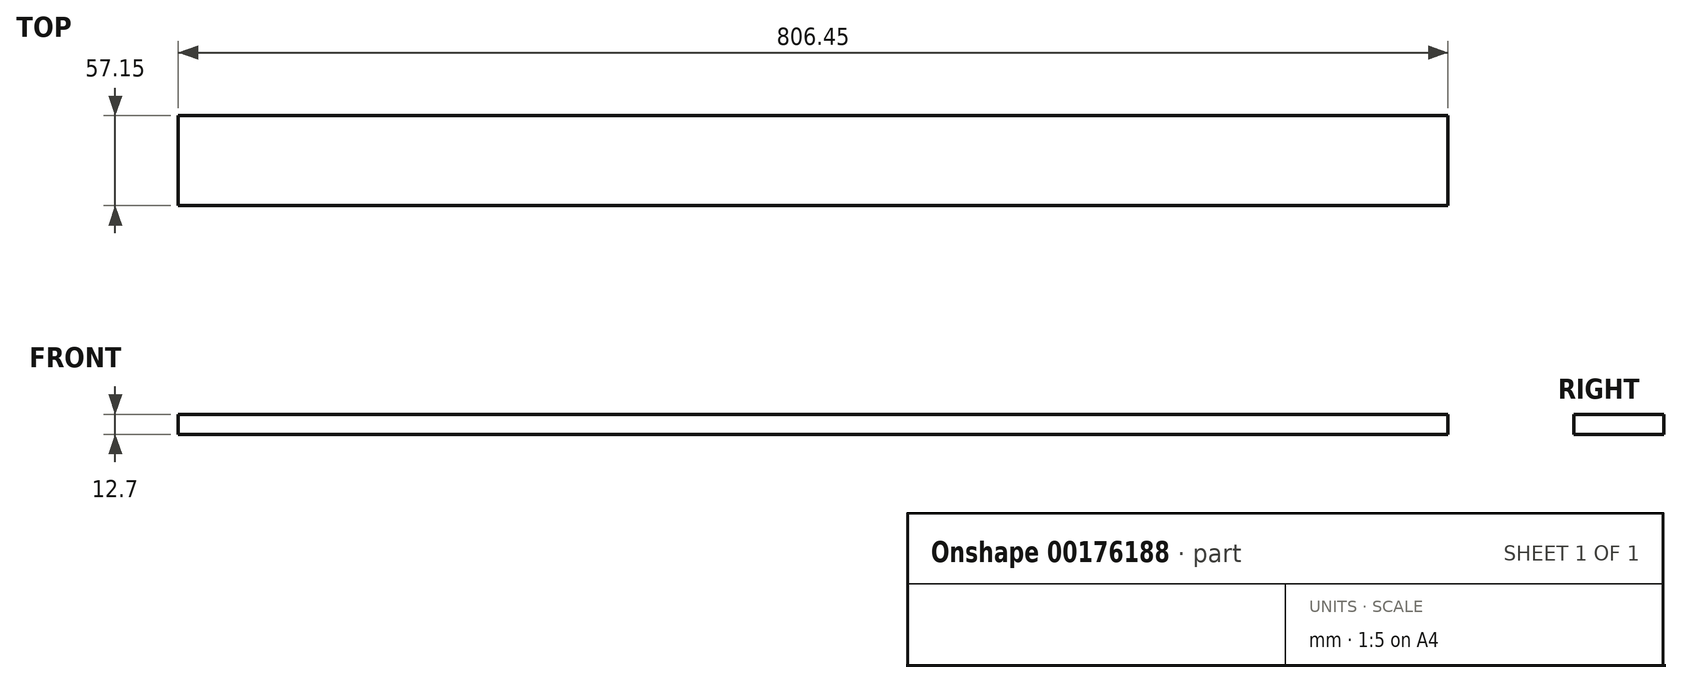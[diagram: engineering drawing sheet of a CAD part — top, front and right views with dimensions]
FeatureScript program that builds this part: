
annotation { "Feature Type Name" : "Feature", "Feature Type Description" : "" }
export const myFeature = defineFeature(function(context is Context, id is Id, definition is map)
    precondition{}
    {
        {
            var Q0;
            Q0=qCreatedBy(makeId("Top.planeOp"),FACE);
            var sketch = newSketch(context, id + "F0", { "sketchPlane" : qUnion([Q0])});
            skLineSegment(sketch, "E0.bottom", {"start": v(0, 0) * mm, "end": v(806.45, 0) * mm});
            skLineSegment(sketch, "E0.top", {"start": v(0, 57.15) * mm, "end": v(806.45, 57.15) * mm});
            skLineSegment(sketch, "E0.left", {"start": v(0, 0) * mm, "end": v(0, 57.15) * mm});
            skLineSegment(sketch, "E0.right", {"start": v(806.45, 0) * mm, "end": v(806.45, 57.15) * mm});
            skSolve(sketch);
        }
        {
            var Q0;
            Q0=makeQuery(id+"F0.imprint","IMPRINT",FACE,{"disambiguationData":[TD([[makeQuery(id+"F0.imprint","IMPRINT",EDGE,{"derivedFrom":sQuery(id+"F0.wireOp",EDGE,"E0.bottom")}),1.0]])]});
            extrude(context, id + "F1", {"entities" : qUnion([Q0]), "depth" : 12.7 * mm});
        }
    });
